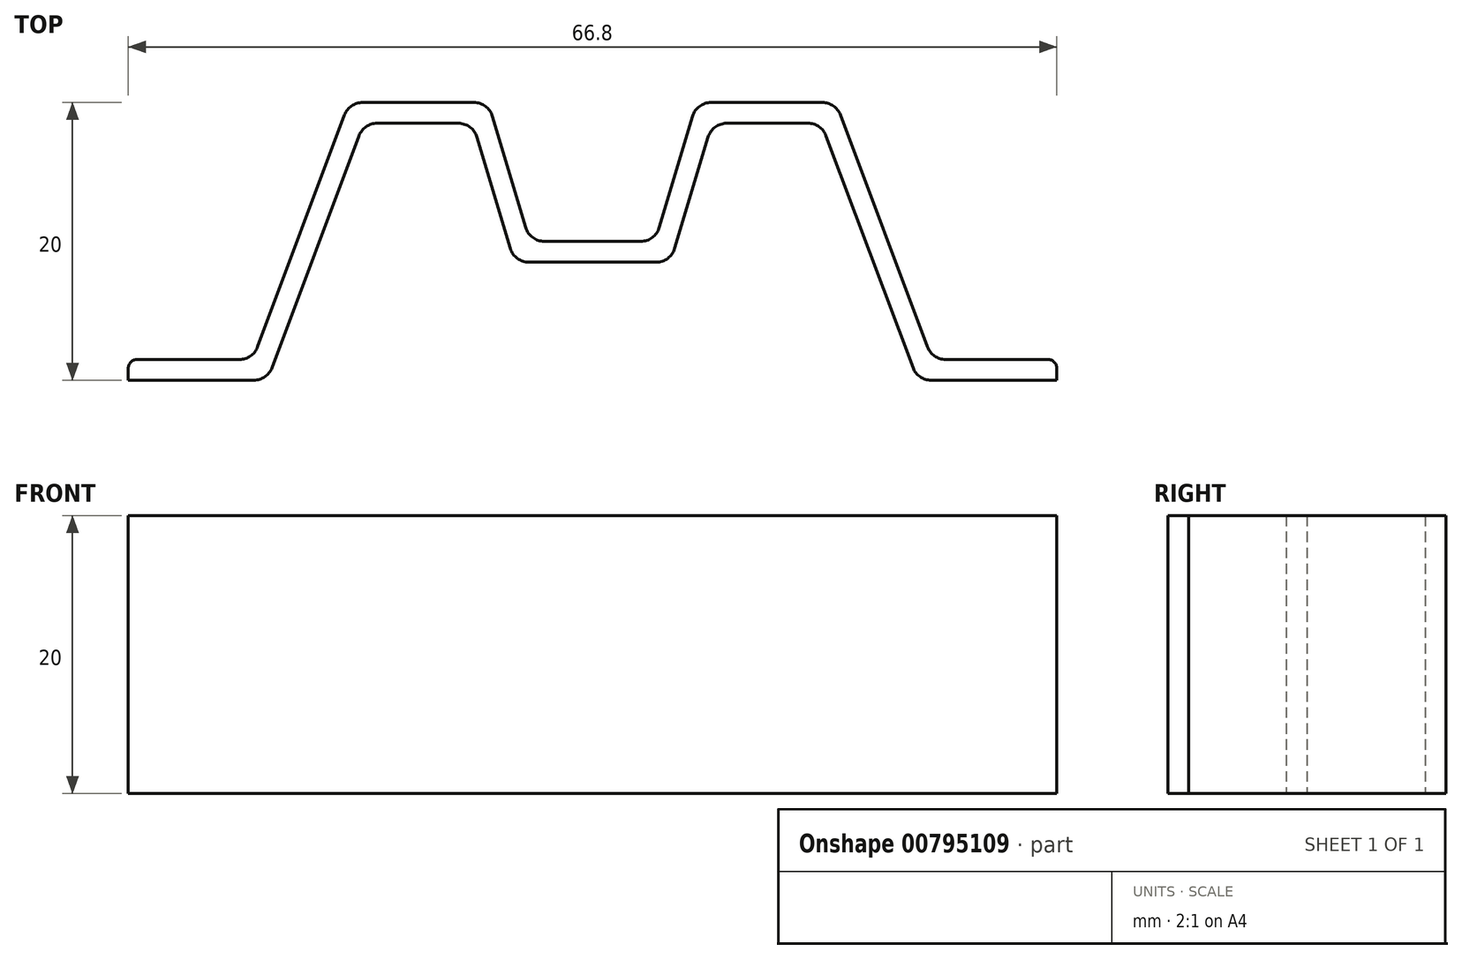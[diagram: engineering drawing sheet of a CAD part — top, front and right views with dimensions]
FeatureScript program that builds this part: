
annotation { "Feature Type Name" : "Feature", "Feature Type Description" : "" }
export const myFeature = defineFeature(function(context is Context, id is Id, definition is map)
    precondition{}
    {
        {
            var Q0;
            Q0=qCreatedBy(makeId("Top.planeOp"),FACE);
            var sketch = newSketch(context, id + "F0", { "sketchPlane" : qUnion([Q0])});
            skLineSegment(sketch, "E0", {"start": v(0, 0) * mm, "end": v(-4.5, 0) * mm});
            skLineSegment(sketch, "E1", {"start": v(-4.5, 0) * mm, "end": v(-4.5, 10) * mm});
            skLineSegment(sketch, "E2", {"start": v(0, 10) * mm, "end": v(-7.5, 10) * mm});
            skLineSegment(sketch, "E3", {"start": v(-7.5, 10) * mm, "end": v(-4.5, 0) * mm});
            skLineSegment(sketch, "E4", {"start": v(-7.5, 10) * mm, "end": v(-17.5, 10) * mm});
            skLineSegment(sketch, "E5", {"start": v(0, 0) * mm, "end": v(0, -10) * mm});
            skLineSegment(sketch, "E6", {"start": v(0, -10) * mm, "end": v(-25, -10) * mm});
            skLineSegment(sketch, "E7", {"start": v(-24.44, -8.5) * mm, "end": v(-17.5, 10) * mm});
            skLineSegment(sketch, "E8.4", {"start": v(-23.4, -10) * mm, "end": v(-16.46, 8.5) * mm});
            skLineSegment(sketch, "E8.5", {"start": v(-8.62, 8.5) * mm, "end": v(-16.46, 8.5) * mm});
            skLineSegment(sketch, "E8.6", {"start": v(-8.62, 8.5) * mm, "end": v(-5.62, -1.5) * mm});
            skLineSegment(sketch, "E8.7", {"start": v(0, -1.5) * mm, "end": v(-5.62, -1.5) * mm});
            skLineSegment(sketch, "E9", {"start": v(-23.4, -10) * mm, "end": v(-33.4, -10) * mm});
            skLineSegment(sketch, "E10.0", {"start": v(-24.44, -8.5) * mm, "end": v(-33.4, -8.5) * mm});
            skLineSegment(sketch, "E11", {"start": v(-33.4, -8.5) * mm, "end": v(-33.4, -10) * mm});
            skLineSegment(sketch, "E12.MirrorCS", {"start": v(0, -1.5) * mm, "end": v(5.62, -1.5) * mm});
            skLineSegment(sketch, "E13.MirrorCS", {"start": v(8.62, 8.5) * mm, "end": v(5.62, -1.5) * mm});
            skLineSegment(sketch, "E14.MirrorCS", {"start": v(0, 0) * mm, "end": v(4.5, 0) * mm});
            skLineSegment(sketch, "E15.MirrorCS", {"start": v(7.5, 10) * mm, "end": v(4.5, 0) * mm});
            skLineSegment(sketch, "E16.MirrorCS", {"start": v(8.62, 8.5) * mm, "end": v(16.46, 8.5) * mm});
            skLineSegment(sketch, "E17.MirrorCS", {"start": v(7.5, 10) * mm, "end": v(17.5, 10) * mm});
            skLineSegment(sketch, "E18.MirrorCS", {"start": v(24.44, -8.5) * mm, "end": v(17.5, 10) * mm});
            skLineSegment(sketch, "E19.MirrorCS", {"start": v(23.4, -10) * mm, "end": v(16.46, 8.5) * mm});
            skLineSegment(sketch, "E20.MirrorCS", {"start": v(23.4, -10) * mm, "end": v(33.4, -10) * mm});
            skLineSegment(sketch, "E21.MirrorCS", {"start": v(24.44, -8.5) * mm, "end": v(33.4, -8.5) * mm});
            skLineSegment(sketch, "E22.MirrorCS", {"start": v(33.4, -8.5) * mm, "end": v(33.4, -10) * mm});
            skSolve(sketch);
        }
        {
            var Q0;
            Q0=makeQuery(id+"F0.imprint","IMPRINT",FACE,{"disambiguationData":[TD([[makeQuery(id+"F0.imprint","IMPRINT",EDGE,{"derivedFrom":sQuery(id+"F0.wireOp",EDGE,"E0")}),1.0]])]});
            var Q1;
            {var subQ0=sQuery(id+"F0.wireOp",EDGE,"3cea7660-3ea7-4f36-8d6f-490685dcf5280.MirrorCS");Q1=makeQuery(id+"F0.imprint","IMPRINT",FACE,{"disambiguationData":[TD([[makeQuery(id+"F0.imprint","IMPRINT",EDGE,{"derivedFrom":subQ0}),1.0]])]});}
            var Q2;
            {var subQ2=sQuery(id+"F0.wireOp",EDGE,"E12.MirrorCS");Q2=makeQuery(id+"F0.imprint","IMPRINT",FACE,{"disambiguationData":[TD([[makeQuery(id+"F0.imprint","IMPRINT",EDGE,{"derivedFrom":subQ2}),1.0]])]});}
            extrude(context, id + "F1", {"entities" : qUnion([Q0, Q1, Q2]), "depth" : 20 * mm, "offsetDistance" : 25 * mm});
        }
        {
            var Q0;
            Q0=makeQuery(id+"F1.opExtrude","SWEPT_EDGE",EDGE,{"disambiguationData":[OSD([sQuery(id+"F0.wireOp",EDGE,"E2"),sQuery(id+"F0.wireOp",EDGE,"E3"),sQuery(id+"F0.wireOp",EDGE,"E4")])]});
            var Q1;
            Q1=makeQuery(id+"F1.opExtrude","SWEPT_EDGE",EDGE,{"disambiguationData":[OSD([sQuery(id+"F0.wireOp",EDGE,"E0"),sQuery(id+"F0.wireOp",EDGE,"E1"),sQuery(id+"F0.wireOp",EDGE,"E3")])]});
            var Q2;
            Q2=makeQuery(id+"F1.opExtrude","SWEPT_EDGE",EDGE,{"disambiguationData":[OSD([sQuery(id+"F0.wireOp",EDGE,"125648d4-1b0f-42f6-8ce5-21553ec1ab010.MirrorCS"),sQuery(id+"F0.wireOp",EDGE,"6c2da147-3f99-4b9b-9460-df8b8448273b0.MirrorCS")])]});
            var Q3;
            Q3=makeQuery(id+"F1.opExtrude","SWEPT_EDGE",EDGE,{"disambiguationData":[OSD([sQuery(id+"F0.wireOp",EDGE,"283f3c24-906e-4047-839c-3c232ed79d660.MirrorCS"),sQuery(id+"F0.wireOp",EDGE,"125648d4-1b0f-42f6-8ce5-21553ec1ab010.MirrorCS")])]});
            var Q4;
            Q4=makeQuery(id+"F1.opExtrude","SWEPT_EDGE",EDGE,{"disambiguationData":[OSD([sQuery(id+"F0.wireOp",EDGE,"E4"),sQuery(id+"F0.wireOp",EDGE,"E7")])]});
            var Q5;
            Q5=makeQuery(id+"F1.opExtrude","SWEPT_EDGE",EDGE,{"disambiguationData":[OSD([sQuery(id+"F0.wireOp",EDGE,"3cea7660-3ea7-4f36-8d6f-490685dcf5280.MirrorCS"),sQuery(id+"F0.wireOp",EDGE,"283f3c24-906e-4047-839c-3c232ed79d660.MirrorCS")])]});
            var Q6;
            Q6=makeQuery(id+"F1.opExtrude","SWEPT_EDGE",EDGE,{"disambiguationData":[OSD([sQuery(id+"F0.wireOp",EDGE,"E8.4"),sQuery(id+"F0.wireOp",EDGE,"E8.5")])]});
            var Q7;
            Q7=makeQuery(id+"F1.opExtrude","SWEPT_EDGE",EDGE,{"disambiguationData":[OSD([sQuery(id+"F0.wireOp",EDGE,"E8.5"),sQuery(id+"F0.wireOp",EDGE,"E8.6")])]});
            var Q8;
            Q8=makeQuery(id+"F1.opExtrude","SWEPT_EDGE",EDGE,{"disambiguationData":[OSD([sQuery(id+"F0.wireOp",EDGE,"E8.6"),sQuery(id+"F0.wireOp",EDGE,"E8.7")])]});
            var Q9;
            Q9=makeQuery(id+"F1.opExtrude","SWEPT_EDGE",EDGE,{"disambiguationData":[OSD([sQuery(id+"F0.wireOp",EDGE,"E8.2"),sQuery(id+"F0.wireOp",EDGE,"E8.3")])]});
            var Q10;
            Q10=makeQuery(id+"F1.opExtrude","SWEPT_EDGE",EDGE,{"disambiguationData":[OSD([sQuery(id+"F0.wireOp",EDGE,"E8.1"),sQuery(id+"F0.wireOp",EDGE,"E8.2")])]});
            var Q11;
            Q11=makeQuery(id+"F1.opExtrude","SWEPT_EDGE",EDGE,{"disambiguationData":[OSD([sQuery(id+"F0.wireOp",EDGE,"E8.0"),sQuery(id+"F0.wireOp",EDGE,"E8.1")])]});
            var Q12;
            Q12=makeQuery(id+"F1.opExtrude","SWEPT_EDGE",EDGE,{"disambiguationData":[OSD([sQuery(id+"F0.wireOp",EDGE,"E17.MirrorCS"),sQuery(id+"F0.wireOp",EDGE,"E18.MirrorCS")])]});
            var Q13;
            Q13=makeQuery(id+"F1.opExtrude","SWEPT_EDGE",EDGE,{"disambiguationData":[OSD([sQuery(id+"F0.wireOp",EDGE,"E15.MirrorCS"),sQuery(id+"F0.wireOp",EDGE,"E17.MirrorCS")])]});
            var Q14;
            Q14=makeQuery(id+"F1.opExtrude","SWEPT_EDGE",EDGE,{"disambiguationData":[OSD([sQuery(id+"F0.wireOp",EDGE,"E14.MirrorCS"),sQuery(id+"F0.wireOp",EDGE,"E15.MirrorCS")])]});
            var Q15;
            Q15=makeQuery(id+"F1.opExtrude","SWEPT_EDGE",EDGE,{"disambiguationData":[OSD([sQuery(id+"F0.wireOp",EDGE,"E18.MirrorCS"),sQuery(id+"F0.wireOp",EDGE,"E21.MirrorCS")])]});
            var Q16;
            Q16=makeQuery(id+"F1.opExtrude","SWEPT_EDGE",EDGE,{"disambiguationData":[OSD([sQuery(id+"F0.wireOp",EDGE,"E7"),sQuery(id+"F0.wireOp",EDGE,"E10.0")])]});
            var Q17;
            Q17=makeQuery(id+"F1.opExtrude","SWEPT_EDGE",EDGE,{"disambiguationData":[OSD([sQuery(id+"F0.wireOp",EDGE,"E12.MirrorCS"),sQuery(id+"F0.wireOp",EDGE,"E13.MirrorCS")])]});
            var Q18;
            Q18=makeQuery(id+"F1.opExtrude","SWEPT_EDGE",EDGE,{"disambiguationData":[OSD([sQuery(id+"F0.wireOp",EDGE,"E13.MirrorCS"),sQuery(id+"F0.wireOp",EDGE,"E16.MirrorCS")])]});
            var Q19;
            Q19=makeQuery(id+"F1.opExtrude","SWEPT_EDGE",EDGE,{"disambiguationData":[OSD([sQuery(id+"F0.wireOp",EDGE,"E16.MirrorCS"),sQuery(id+"F0.wireOp",EDGE,"E19.MirrorCS")])]});
            var Q20;
            Q20=makeQuery(id+"F1.opExtrude","SWEPT_EDGE",EDGE,{"disambiguationData":[OSD([sQuery(id+"F0.wireOp",EDGE,"E19.MirrorCS"),sQuery(id+"F0.wireOp",EDGE,"E20.MirrorCS")])]});
            var Q21;
            Q21=makeQuery(id+"F1.opExtrude","SWEPT_EDGE",EDGE,{"disambiguationData":[OSD([sQuery(id+"F0.wireOp",EDGE,"E6"),sQuery(id+"F0.wireOp",EDGE,"E8.4"),sQuery(id+"F0.wireOp",EDGE,"E9")])]});
            fillet(context, id + "F2", {"entities" : qUnion([Q0, Q1, Q2, Q3, Q4, Q5, Q6, Q7, Q8, Q9, Q10, Q11, Q12, Q13, Q14, Q15, Q16, Q17, Q18, Q19, Q20, Q21]), "radius" : 1.38 * mm, "tangentPropagation" : true, "allowEdgeOverflow" : false});
        }
        {
            var Q0;
            Q0=makeQuery(id+"FmpHjSiWCrfygaJ_1.boolean.opBoolean","INTERSECT",EDGE,{"disambiguationData":[OD(1.0)],"derivedFrom":[makeQuery(id+"F1.opExtrude","SWEPT_FACE",FACE,{"disambiguationData":[OSD([sQuery(id+"F0.wireOp",EDGE,"E6")])]}),makeQuery(id+"FmpHjSiWCrfygaJ_1.opExtrude","SWEPT_FACE",FACE,{"disambiguationData":[OSD([sQuery(id+"FOfNdHXlx8KAovd_1.wireOp",EDGE,"JhGbhF74-61kD-nXkE-BUDY-nQiPn96c632G")])]})]});
            var Q1;
            Q1=makeQuery(id+"FmpHjSiWCrfygaJ_1.boolean.opBoolean","INTERSECT",EDGE,{"disambiguationData":[OD(0.0)],"derivedFrom":[makeQuery(id+"F1.opExtrude","SWEPT_FACE",FACE,{"disambiguationData":[OSD([sQuery(id+"F0.wireOp",EDGE,"E6")])]}),makeQuery(id+"FmpHjSiWCrfygaJ_1.opExtrude","SWEPT_FACE",FACE,{"disambiguationData":[OSD([sQuery(id+"FOfNdHXlx8KAovd_1.wireOp",EDGE,"JhGbhF74-61kD-nXkE-BUDY-nQiPn96c632G")])]})]});
            var Q2;
            Q2=makeQuery(id+"FmpHjSiWCrfygaJ_1.boolean.opBoolean","INTERSECT",EDGE,{"disambiguationData":[OD(0.0)],"derivedFrom":[makeQuery(id+"F1.opExtrude","SWEPT_FACE",FACE,{"disambiguationData":[OSD([sQuery(id+"F0.wireOp",EDGE,"23547863-f32c-4499-9e2e-89fceff4eab40.MirrorCS")])]}),makeQuery(id+"FmpHjSiWCrfygaJ_1.opExtrude","SWEPT_FACE",FACE,{"disambiguationData":[OSD([sQuery(id+"FOfNdHXlx8KAovd_1.wireOp",EDGE,"JhGbhF74-61kD-nXkE-BUDY-nQiPn96c632G")])]})]});
            var Q3;
            Q3=makeQuery(id+"FmpHjSiWCrfygaJ_1.boolean.opBoolean","INTERSECT",EDGE,{"disambiguationData":[OD(1.0)],"derivedFrom":[makeQuery(id+"F1.opExtrude","SWEPT_FACE",FACE,{"disambiguationData":[OSD([sQuery(id+"F0.wireOp",EDGE,"23547863-f32c-4499-9e2e-89fceff4eab40.MirrorCS")])]}),makeQuery(id+"FmpHjSiWCrfygaJ_1.opExtrude","SWEPT_FACE",FACE,{"disambiguationData":[OSD([sQuery(id+"FOfNdHXlx8KAovd_1.wireOp",EDGE,"JhGbhF74-61kD-nXkE-BUDY-nQiPn96c632G")])]})]});
            var Q4;
            Q4=makeQuery(id+"F1.opExtrude","SWEPT_EDGE",EDGE,{"disambiguationData":[OSD([sQuery(id+"F0.wireOp",EDGE,"E10.0"),sQuery(id+"F0.wireOp",EDGE,"E11")])]});
            var Q5;
            Q5=makeQuery(id+"F1.opExtrude","SWEPT_EDGE",EDGE,{"disambiguationData":[OSD([sQuery(id+"F0.wireOp",EDGE,"E21.MirrorCS"),sQuery(id+"F0.wireOp",EDGE,"E22.MirrorCS")])]});
            fillet(context, id + "F3", {"entities" : qUnion([Q0, Q1, Q2, Q3, Q4, Q5]), "radius" : 0.64 * mm, "tangentPropagation" : true, "allowEdgeOverflow" : false});
        }
    });
